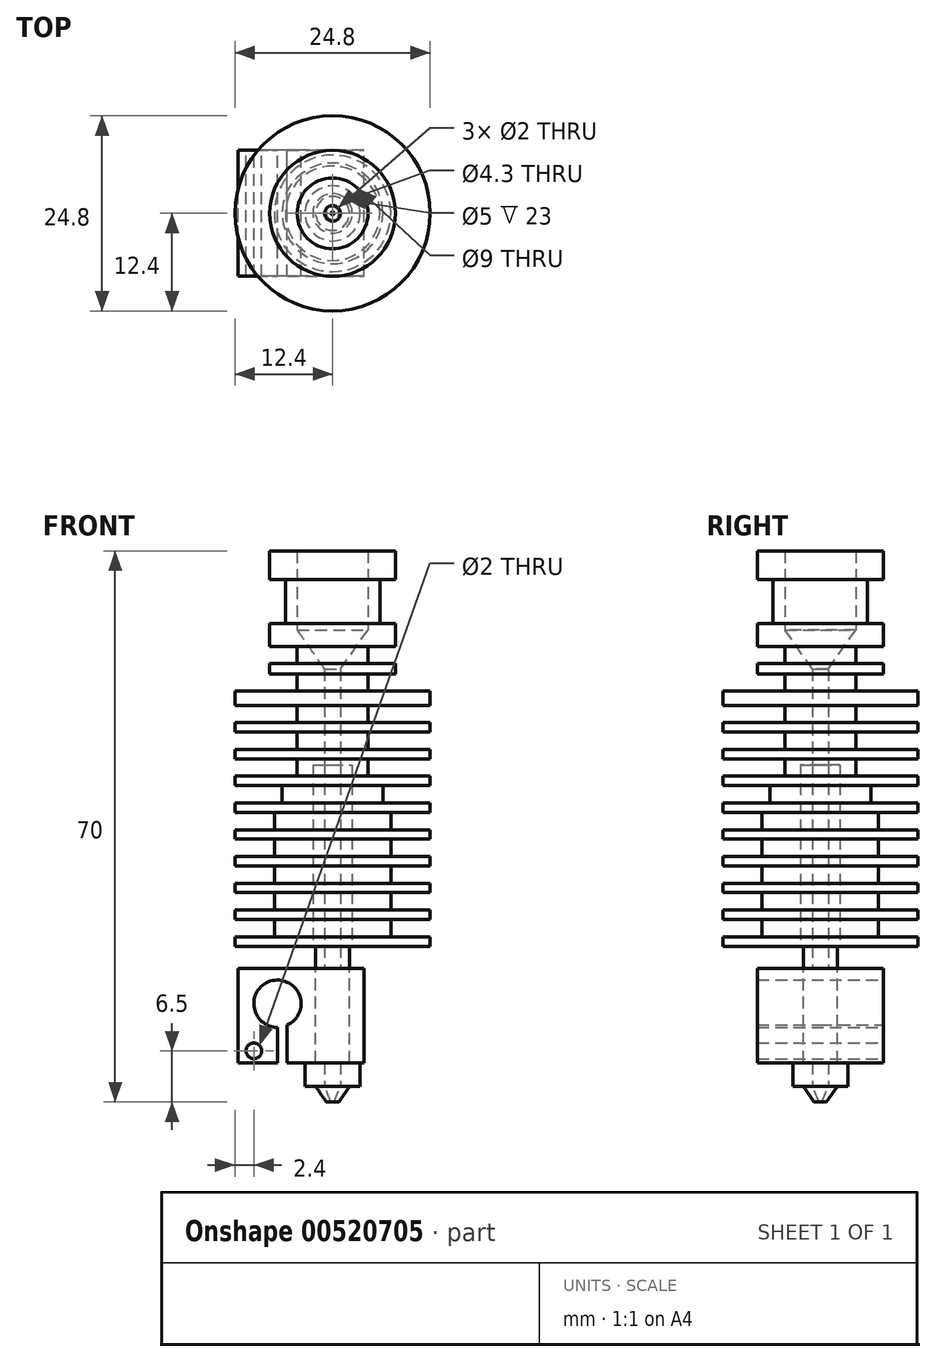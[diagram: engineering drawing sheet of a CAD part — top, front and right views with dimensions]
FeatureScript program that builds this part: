
annotation { "Feature Type Name" : "Feature", "Feature Type Description" : "" }
export const myFeature = defineFeature(function(context is Context, id is Id, definition is map)
    precondition{}
    {
        {
            var Q0;
            Q0=qCreatedBy(makeId("Front.planeOp"),FACE);
            var sketch = newSketch(context, id + "F0", { "sketchPlane" : qUnion([Q0])});
            skLineSegment(sketch, "E0", {"start": v(0, 0) * mm, "end": v(2.5, 0) * mm, "construction": true});
            skLineSegment(sketch, "E1", {"start": v(2.5, 0) * mm, "end": v(12.4, 0) * mm});
            skLineSegment(sketch, "E2", {"start": v(12.4, 0) * mm, "end": v(12.4, 1.2) * mm});
            skLineSegment(sketch, "E3", {"start": v(12.4, 1.2) * mm, "end": v(7.4, 1.2) * mm});
            skLineSegment(sketch, "E4", {"start": v(7.4, 1.2) * mm, "end": v(7.4, 3.4) * mm});
            skLineSegment(sketch, "E5", {"start": v(7.4, 3.4) * mm, "end": v(12.4, 3.4) * mm});
            skLineSegment(sketch, "E6", {"start": v(12.4, 3.4) * mm, "end": v(12.4, 4.6) * mm});
            skLineSegment(sketch, "E7", {"start": v(12.4, 4.6) * mm, "end": v(7.4, 4.6) * mm});
            skLineSegment(sketch, "E8", {"start": v(7.4, 4.6) * mm, "end": v(7.4, 6.8) * mm});
            skLineSegment(sketch, "E9", {"start": v(7.4, 6.8) * mm, "end": v(12.4, 6.8) * mm});
            skLineSegment(sketch, "E10", {"start": v(12.4, 6.8) * mm, "end": v(12.4, 8) * mm});
            skLineSegment(sketch, "E11", {"start": v(12.4, 8) * mm, "end": v(7.4, 8) * mm});
            skLineSegment(sketch, "E12", {"start": v(7.4, 8) * mm, "end": v(7.4, 10.2) * mm});
            skLineSegment(sketch, "E13", {"start": v(7.4, 10.2) * mm, "end": v(12.4, 10.2) * mm});
            skLineSegment(sketch, "E14", {"start": v(12.4, 10.2) * mm, "end": v(12.4, 11.4) * mm});
            skLineSegment(sketch, "E15", {"start": v(12.4, 11.4) * mm, "end": v(7.4, 11.4) * mm});
            skLineSegment(sketch, "E16", {"start": v(7.4, 11.4) * mm, "end": v(7.4, 13.6) * mm});
            skLineSegment(sketch, "E17", {"start": v(7.4, 13.6) * mm, "end": v(12.4, 13.6) * mm});
            skLineSegment(sketch, "E18", {"start": v(12.4, 13.6) * mm, "end": v(12.4, 14.8) * mm});
            skLineSegment(sketch, "E19", {"start": v(12.4, 14.8) * mm, "end": v(7.4, 14.8) * mm});
            skLineSegment(sketch, "E20", {"start": v(7.4, 14.8) * mm, "end": v(7.4, 17) * mm});
            skLineSegment(sketch, "E21", {"start": v(7.4, 17) * mm, "end": v(12.4, 17) * mm});
            skLineSegment(sketch, "E22", {"start": v(12.4, 17) * mm, "end": v(12.4, 18.2) * mm});
            skLineSegment(sketch, "E23", {"start": v(12.4, 18.2) * mm, "end": v(6.4, 18.2) * mm});
            skLineSegment(sketch, "E24", {"start": v(6.4, 18.2) * mm, "end": v(6.4, 20.4) * mm});
            skLineSegment(sketch, "E25", {"start": v(6.4, 20.4) * mm, "end": v(12.4, 20.4) * mm});
            skLineSegment(sketch, "E26", {"start": v(12.4, 20.4) * mm, "end": v(12.4, 21.6) * mm});
            skLineSegment(sketch, "E27", {"start": v(12.4, 21.6) * mm, "end": v(4.5, 21.6) * mm});
            skLineSegment(sketch, "E28", {"start": v(4.5, 21.6) * mm, "end": v(4.5, 23.8) * mm});
            skLineSegment(sketch, "E29", {"start": v(4.5, 23.8) * mm, "end": v(12.4, 23.8) * mm});
            skLineSegment(sketch, "E30", {"start": v(12.4, 23.8) * mm, "end": v(12.4, 25) * mm});
            skLineSegment(sketch, "E31", {"start": v(12.4, 25) * mm, "end": v(4.5, 25) * mm});
            skLineSegment(sketch, "E32", {"start": v(4.5, 25) * mm, "end": v(4.5, 27.2) * mm});
            skLineSegment(sketch, "E33", {"start": v(4.5, 27.2) * mm, "end": v(12.4, 27.2) * mm});
            skLineSegment(sketch, "E34", {"start": v(12.4, 27.2) * mm, "end": v(12.4, 28.4) * mm});
            skLineSegment(sketch, "E35", {"start": v(12.4, 28.4) * mm, "end": v(4.5, 28.4) * mm});
            skLineSegment(sketch, "E36", {"start": v(4.5, 28.4) * mm, "end": v(4.5, 30.6) * mm});
            skLineSegment(sketch, "E37", {"start": v(4.5, 30.6) * mm, "end": v(12.4, 30.6) * mm});
            skLineSegment(sketch, "E38", {"start": v(12.4, 30.6) * mm, "end": v(12.4, 32.4) * mm});
            skLineSegment(sketch, "E39", {"start": v(12.4, 32.4) * mm, "end": v(4.5, 32.4) * mm});
            skLineSegment(sketch, "E40", {"start": v(4.5, 32.4) * mm, "end": v(4.5, 34.6) * mm});
            skLineSegment(sketch, "E41", {"start": v(4.5, 34.6) * mm, "end": v(8, 34.6) * mm});
            skLineSegment(sketch, "E42", {"start": v(8, 34.6) * mm, "end": v(8, 35.9) * mm});
            skLineSegment(sketch, "E43", {"start": v(8, 35.9) * mm, "end": v(4.5, 35.9) * mm});
            skLineSegment(sketch, "E44", {"start": v(4.5, 35.9) * mm, "end": v(4.5, 38.1) * mm});
            skLineSegment(sketch, "E45", {"start": v(4.5, 38.1) * mm, "end": v(8, 38.1) * mm});
            skLineSegment(sketch, "E46", {"start": v(8, 38.1) * mm, "end": v(8, 41) * mm});
            skLineSegment(sketch, "E47", {"start": v(8, 41) * mm, "end": v(6, 41) * mm});
            skLineSegment(sketch, "E48", {"start": v(6, 41) * mm, "end": v(6, 46.6) * mm});
            skLineSegment(sketch, "E49", {"start": v(6, 46.6) * mm, "end": v(8, 46.6) * mm});
            skLineSegment(sketch, "E50", {"start": v(8, 46.6) * mm, "end": v(8, 50.2) * mm});
            skLineSegment(sketch, "E51", {"start": v(8, 50.2) * mm, "end": v(4.5, 50.2) * mm});
            skLineSegment(sketch, "E52", {"start": v(4.5, 50.2) * mm, "end": v(4.5, 40.2) * mm});
            skLineSegment(sketch, "E53", {"start": v(4.5, 40.2) * mm, "end": v(1, 35.2) * mm});
            skLineSegment(sketch, "E54", {"start": v(2.5, 0) * mm, "end": v(2.5, 23) * mm});
            skLineSegment(sketch, "E55", {"start": v(1, 23) * mm, "end": v(1, 35.2) * mm});
            skLineSegment(sketch, "E56", {"start": v(2.5, 23) * mm, "end": v(1, 23) * mm});
            skLineSegment(sketch, "E57", {"start": v(0, 0) * mm, "end": v(0, 59.05) * mm, "construction": true});
            skLineSegment(sketch, "E58", {"start": v(1, 23) * mm, "end": v(1, 0) * mm});
            skLineSegment(sketch, "E59", {"start": v(1, 0) * mm, "end": v(1, -7.3) * mm});
            skLineSegment(sketch, "E60", {"start": v(1, -7.3) * mm, "end": v(2.15, -7.3) * mm});
            skLineSegment(sketch, "E61", {"start": v(2.15, -7.3) * mm, "end": v(2.15, 0) * mm});
            skLineSegment(sketch, "E62", {"start": v(2.15, 0) * mm, "end": v(2.5, 0) * mm});
            skLineSegment(sketch, "E63", {"start": v(1, -7.3) * mm, "end": v(1, -17.8) * mm});
            skLineSegment(sketch, "E64", {"start": v(1, -17.8) * mm, "end": v(0.2, -19.8) * mm});
            skLineSegment(sketch, "E65", {"start": v(0.2, -19.8) * mm, "end": v(0.8, -19.8) * mm});
            skLineSegment(sketch, "E66", {"start": v(2.15, -17.8) * mm, "end": v(0.8, -19.8) * mm});
            skLineSegment(sketch, "E67", {"start": v(2.15, -17.8) * mm, "end": v(3.5, -17.8) * mm});
            skLineSegment(sketch, "E68", {"start": v(3.5, -17.8) * mm, "end": v(3.5, -14.8) * mm});
            skLineSegment(sketch, "E69", {"start": v(3.5, -14.8) * mm, "end": v(2.15, -14.8) * mm});
            skLineSegment(sketch, "E70", {"start": v(2.15, -14.8) * mm, "end": v(2.15, -7.3) * mm});
            skLineSegment(sketch, "E71", {"start": v(3.5, -14.8) * mm, "end": v(4, -14.8) * mm});
            skLineSegment(sketch, "E72", {"start": v(4, -14.8) * mm, "end": v(4, -2.8) * mm});
            skLineSegment(sketch, "E73", {"start": v(4, -2.8) * mm, "end": v(-12, -2.8) * mm});
            skLineSegment(sketch, "E74", {"start": v(-12, -2.8) * mm, "end": v(-12, -14.8) * mm});
            skLineSegment(sketch, "E75", {"start": v(-12, -14.8) * mm, "end": v(2.15, -14.8) * mm});
            skLineSegment(sketch, "E76", {"start": v(0, -2.8) * mm, "end": v(0, -14.8) * mm});
            skCircle(sketch, "E77", {"center": v(-7, -7.3) * mm, "radius": 3 * mm});
            skCircle(sketch, "E78", {"center": v(-10, -13.3) * mm, "radius": 1 * mm});
            skLineSegment(sketch, "E79", {"start": v(-7, -7.3) * mm, "end": v(-7, -14.8) * mm});
            skLineSegment(sketch, "E80", {"start": v(-7, -14.8) * mm, "end": v(-5.75, -14.8) * mm});
            skLineSegment(sketch, "E81", {"start": v(-5.75, -14.8) * mm, "end": v(-5.75, -7.3) * mm});
            skLineSegment(sketch, "E82", {"start": v(-5.75, -7.3) * mm, "end": v(-7, -7.3) * mm});
            skSolve(sketch);
        }
        {
            var Q0;
            Q0=makeQuery(id+"F0.imprint","IMPRINT",FACE,{"disambiguationData":[TD([[makeQuery(id+"F0.imprint","IMPRINT",EDGE,{"derivedFrom":sQuery(id+"F0.wireOp",EDGE,"E1")}),1.0]])]});
            var Q1;
            Q1=sQuery(id+"F0.wireOp",EDGE,"E57");
            revolve(context, id + "F1", {"entities" : qUnion([Q0]), "axis" : qUnion([Q1]), "revolveType" : RevolveType.FULL});
        }
        {
            var Q0;
            Q0=makeQuery(id+"F0.imprint","IMPRINT",FACE,{"disambiguationData":[TD([[makeQuery(id+"F0.imprint","IMPRINT",EDGE,{"derivedFrom":sQuery(id+"F0.wireOp",EDGE,"E54")}),1.0]])]});
            var Q1;
            Q1=sQuery(id+"F0.wireOp",EDGE,"E57");
            revolve(context, id + "F2", {"entities" : qUnion([Q0]), "axis" : qUnion([Q1]), "revolveType" : RevolveType.FULL});
        }
        {
            var Q0;
            Q0=makeQuery(id+"F0.imprint","IMPRINT",FACE,{"disambiguationData":[TD([[makeQuery(id+"F0.imprint","IMPRINT",EDGE,{"derivedFrom":sQuery(id+"F0.wireOp",EDGE,"E60")}),-1.0]])]});
            var Q1;
            {var subQ0=sQuery(id+"F0.wireOp",EDGE,"E64");Q1=makeQuery(id+"F0.imprint","IMPRINT",FACE,{"disambiguationData":[TD([[makeQuery(id+"F0.imprint","IMPRINT",EDGE,{"derivedFrom":subQ0}),1.0]])]});}
            var Q2;
            {var subQ0=sQuery(id+"F0.wireOp",EDGE,"E60");Q2=makeQuery(id+"F0.imprint","IMPRINT",FACE,{"disambiguationData":[TD([[makeQuery(id+"F0.imprint","IMPRINT",EDGE,{"derivedFrom":subQ0}),1.0]])]});}
            var Q3;
            Q3=sQuery(id+"F0.wireOp",EDGE,"E57");
            revolve(context, id + "F3", {"entities" : qUnion([Q0, Q1, Q2]), "axis" : qUnion([Q3]), "revolveType" : RevolveType.FULL});
        }
        {
            var Q0;
            {var subQ0=sQuery(id+"F0.wireOp",EDGE,"E74");Q0=makeQuery(id+"F0.imprint","IMPRINT",FACE,{"disambiguationData":[TD([[makeQuery(id+"F0.imprint","IMPRINT",EDGE,{"derivedFrom":subQ0}),1.0]])]});}
            var Q1;
            {var subQ0=sQuery(id+"F0.wireOp",EDGE,"E60");Q1=makeQuery(id+"F0.imprint","IMPRINT",FACE,{"disambiguationData":[TD([[makeQuery(id+"F0.imprint","IMPRINT",EDGE,{"derivedFrom":subQ0}),1.0]])]});}
            var Q2;
            Q2=makeQuery(id+"F0.imprint","IMPRINT",FACE,{"disambiguationData":[TD([[makeQuery(id+"F0.imprint","IMPRINT",EDGE,{"derivedFrom":sQuery(id+"F0.wireOp",EDGE,"E69")}),-1.0]])]});
            var Q3;
            {var subQ0=sQuery(id+"F0.wireOp",EDGE,"E60");Q3=makeQuery(id+"F0.imprint","IMPRINT",FACE,{"disambiguationData":[TD([[makeQuery(id+"F0.imprint","IMPRINT",EDGE,{"derivedFrom":subQ0}),-1.0]])]});}
            var Q4;
            {var subQ0=sQuery(id+"F0.wireOp",EDGE,"E76");Q4=makeQuery(id+"F0.imprint","IMPRINT",FACE,{"disambiguationData":[TD([[makeQuery(id+"F0.imprint","IMPRINT",EDGE,{"derivedFrom":subQ0}),1.0]])]});}
            var Q5;
            {var subQ5=sQuery(id+"F0.wireOp",EDGE,"E80");Q5=makeQuery(id+"F0.imprint","IMPRINT",FACE,{"disambiguationData":[TD([[makeQuery(id+"F0.imprint","IMPRINT",EDGE,{"derivedFrom":subQ5}),1.0]])]});}
            extrude(context, id + "F4", {"entities" : qUnion([Q0, Q1, Q2, Q3, Q4, Q5]), "depth" : 8 * mm, "offsetDistance" : 25 * mm, "hasSecondDirection" : true, "secondDirectionOppositeDirection" : true, "secondDirectionDepth" : 8 * mm});
        }
        {
            var Q0;
            {var subQ0=sQuery(id+"F0.wireOp",EDGE,"E76");Q0=makeQuery(id+"F0.imprint","IMPRINT",FACE,{"disambiguationData":[TD([[makeQuery(id+"F0.imprint","IMPRINT",EDGE,{"derivedFrom":subQ0}),1.0]])]});}
            var Q1;
            {var subQ0=sQuery(id+"F0.wireOp",EDGE,"E60");Q1=makeQuery(id+"F0.imprint","IMPRINT",FACE,{"disambiguationData":[TD([[makeQuery(id+"F0.imprint","IMPRINT",EDGE,{"derivedFrom":subQ0}),1.0]])]});}
            var Q2;
            {var subQ0=sQuery(id+"F0.wireOp",EDGE,"E60");Q2=makeQuery(id+"F0.imprint","IMPRINT",FACE,{"disambiguationData":[TD([[makeQuery(id+"F0.imprint","IMPRINT",EDGE,{"derivedFrom":subQ0}),-1.0]])]});}
            var Q3;
            Q3=sQuery(id+"F0.wireOp",EDGE,"E57");
            revolve(context, id + "F5", {"operationType" : NewBodyOperationType.REMOVE, "entities" : qUnion([Q0, Q1, Q2]), "axis" : qUnion([Q3]), "revolveType" : RevolveType.FULL, "oppositeDirection" : true});
        }
        {
            var Q0;
            {var subQ5=sQuery(id+"F0.wireOp",EDGE,"E80");Q0=makeQuery(id+"F0.imprint","IMPRINT",FACE,{"disambiguationData":[TD([[makeQuery(id+"F0.imprint","IMPRINT",EDGE,{"derivedFrom":subQ5}),1.0]])]});}
            var Q1;
            {var subQ5=sQuery(id+"F0.wireOp",EDGE,"E82");Q1=makeQuery(id+"F0.imprint","IMPRINT",FACE,{"disambiguationData":[TD([[makeQuery(id+"F0.imprint","IMPRINT",EDGE,{"derivedFrom":subQ5}),1.0]])]});}
            var Q2;
            Q2=sQuery(id+"F0.wireOp",EDGE,"E79");
            revolve(context, id + "F6", {"operationType" : NewBodyOperationType.REMOVE, "entities" : qUnion([Q0, Q1]), "axis" : qUnion([Q2]), "revolveType" : RevolveType.FULL, "oppositeDirection" : true});
        }
    });
